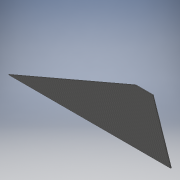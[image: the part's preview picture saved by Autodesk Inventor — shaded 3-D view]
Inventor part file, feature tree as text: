
AUTODESK INVENTOR PART (.ipt)
format: ipt  version: 2017 SP1 (Build 210196100, 196)  size: 97,280 bytes
history: native  units: in
note: dims shown in document units (in); Inventor stores cm internally (conversion verified against a paired STEP export)
features: extrude x1, sketch x1
ambient origin geometry x8: Origin, YZ Plane, XZ Plane, XY Plane, X Axis, Y Axis, Z Axis, Center Point
bodies: Solid1 (feature_tree)
feature tree (2):
  extrude  "Extrusion1"  Depth=0.125in
  sketch  "Sketch1"  dims[d0=24.17in d1=18.88in d2=8.09in d3=2.6in d4=0.125in d5=0.0in]
